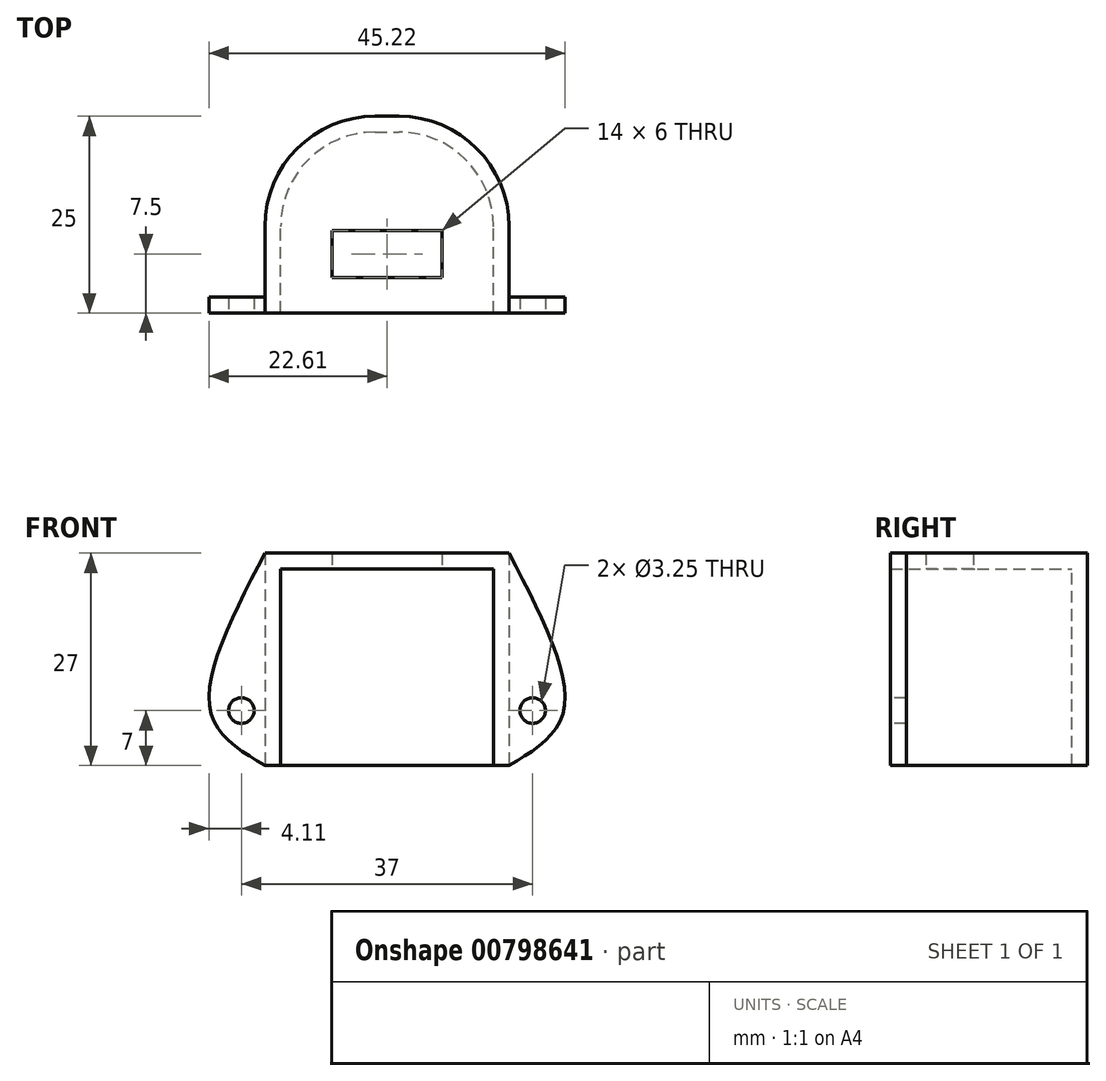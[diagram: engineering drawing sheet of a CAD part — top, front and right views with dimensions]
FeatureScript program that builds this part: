
annotation { "Feature Type Name" : "Feature", "Feature Type Description" : "" }
export const myFeature = defineFeature(function(context is Context, id is Id, definition is map)
    precondition{}
    {
        {
            var Q0;
            Q0=qCreatedBy(makeId("Top.planeOp"),FACE);
            var sketch = newSketch(context, id + "F0", { "sketchPlane" : qUnion([Q0])});
            skLineSegment(sketch, "E0.top", {"start": v(12, 23) * mm, "end": v(15, 23) * mm});
            skLineSegment(sketch, "E0.left", {"start": v(0, 5) * mm, "end": v(0, 11) * mm});
            skLineSegment(sketch, "E0.right", {"start": v(27, 5) * mm, "end": v(27, 11) * mm});
            skPoint(sketch, "E1.visualSharp", {"position": v(0, 23) * mm});
            skArc(sketch, "E1.filletArc", {"start": v(12, 23) * mm, "mid": v(3.51, 19.49) * mm, "end": v(0, 11) * mm});
            skPoint(sketch, "E2.visualSharp", {"position": v(27, 23) * mm});
            skArc(sketch, "E2.filletArc", {"start": v(27, 11) * mm, "mid": v(23.49, 19.49) * mm, "end": v(15, 23) * mm});
            skPoint(sketch, "E3.visualSharp", {"position": v(27, 0) * mm});
            skPoint(sketch, "E4.visualSharp", {"position": v(0, 0) * mm});
            skLineSegment(sketch, "E5.2", {"start": v(-2, 5) * mm, "end": v(-2, 11) * mm});
            skArc(sketch, "E5.4", {"start": v(12, 25) * mm, "mid": v(2.1, 20.9) * mm, "end": v(-2, 11) * mm});
            skLineSegment(sketch, "E5.5", {"start": v(12, 25) * mm, "end": v(15, 25) * mm});
            skArc(sketch, "E5.6", {"start": v(29, 11) * mm, "mid": v(24.9, 20.9) * mm, "end": v(15, 25) * mm});
            skLineSegment(sketch, "E5.7", {"start": v(29, 5) * mm, "end": v(29, 11) * mm});
            skLineSegment(sketch, "E6.bottom", {"start": v(6.5, 10.5) * mm, "end": v(20.5, 10.5) * mm});
            skLineSegment(sketch, "E6.top", {"start": v(6.5, 4.5) * mm, "end": v(20.5, 4.5) * mm});
            skLineSegment(sketch, "E6.left", {"start": v(6.5, 10.5) * mm, "end": v(6.5, 4.5) * mm});
            skLineSegment(sketch, "E6.right", {"start": v(20.5, 10.5) * mm, "end": v(20.5, 4.5) * mm});
            skLineSegment(sketch, "E7", {"start": v(-2, 5) * mm, "end": v(-2, 0) * mm});
            skLineSegment(sketch, "E8", {"start": v(29, 0) * mm, "end": v(29, 5) * mm});
            skLineSegment(sketch, "E9", {"start": v(0, 5) * mm, "end": v(0, 0) * mm});
            skLineSegment(sketch, "E10", {"start": v(0, 0) * mm, "end": v(-2, 0) * mm});
            skLineSegment(sketch, "E11", {"start": v(27, 5) * mm, "end": v(27, 0) * mm});
            skLineSegment(sketch, "E12", {"start": v(27, 0) * mm, "end": v(29, 0) * mm});
            skPoint(sketch, "E13.orphan", {"position": v(29, -2) * mm});
            skLineSegment(sketch, "E14", {"start": v(0, 0) * mm, "end": v(27, 0) * mm});
            skSolve(sketch);
        }
        {
            var Q0;
            Q0=makeQuery(id+"F0.imprint","IMPRINT",FACE,{"disambiguationData":[TD([[makeQuery(id+"F0.imprint","IMPRINT",EDGE,{"derivedFrom":sQuery(id+"F0.wireOp",EDGE,"E0.top")}),1.0]])]});
            var Q1;
            Q1=makeQuery(id+"F0.imprint","IMPRINT",FACE,{"disambiguationData":[TD([[makeQuery(id+"F0.imprint","IMPRINT",EDGE,{"derivedFrom":sQuery(id+"F0.wireOp",EDGE,"E0.top")}),-1.0]])]});
            extrude(context, id + "F1", {"entities" : qUnion([Q0, Q1]), "depth" : 2 * mm, "offsetDistance" : 25 * mm});
        }
        {
            var Q0;
            Q0=makeQuery(id+"F1.opExtrude","CAP_FACE",FACE,{"disambiguationData":[OSD([sQuery(id+"F0.wireOp",EDGE,"E0.bottom"),sQuery(id+"F0.wireOp",EDGE,"E0.top"),sQuery(id+"F0.wireOp",EDGE,"E0.left"),sQuery(id+"F0.wireOp",EDGE,"E0.right"),sQuery(id+"F0.wireOp",EDGE,"E1.filletArc"),sQuery(id+"F0.wireOp",EDGE,"E2.filletArc"),sQuery(id+"F0.wireOp",EDGE,"E6.bottom"),sQuery(id+"F0.wireOp",EDGE,"E6.top"),sQuery(id+"F0.wireOp",EDGE,"E6.left"),sQuery(id+"F0.wireOp",EDGE,"E6.right"),sQuery(id+"F0.wireOp",EDGE,"E9"),sQuery(id+"F0.wireOp",EDGE,"LHaNOpJJ-Fasi-Yn89-1YLt-XwrULM0i3jNw"),sQuery(id+"F0.wireOp",EDGE,"VzsqZfYQ-e0Jo-APly-HRyu-TeHSbx14rwkw"),sQuery(id+"F0.wireOp",EDGE,"E11")])],"isStart":true});
            var sketch = newSketch(context, id + "F2", { "sketchPlane" : qUnion([Q0])});
            skLineSegment(sketch, "E15.0", {"start": v(0, 0) * mm, "end": v(0, -11) * mm});
            skLineSegment(sketch, "E15.1", {"start": v(27, 0) * mm, "end": v(27, -11) * mm});
            skArc(sketch, "E15.2", {"start": v(27, -11) * mm, "mid": v(23.49, -19.49) * mm, "end": v(15, -23) * mm});
            skLineSegment(sketch, "E15.3", {"start": v(12, -23) * mm, "end": v(15, -23) * mm});
            skArc(sketch, "E15.4", {"start": v(12, -23) * mm, "mid": v(3.51, -19.49) * mm, "end": v(0, -11) * mm});
            skSolve(sketch);
        }
        {
            var Q0;
            {var subQ2=sQuery(id+"F2.wireOp",EDGE,"E15.0");Q0=makeQuery(id+"F2.imprint","IMPRINT",FACE,{"disambiguationData":[TD([[makeQuery(id+"F2.imprint","IMPRINT",EDGE,{"derivedFrom":subQ2}),-1.0]])]});}
            extrude(context, id + "F3", {"entities" : qUnion([Q0]), "operationType" : NewBodyOperationType.ADD, "depth" : 25 * mm, "offsetDistance" : 25 * mm});
        }
        {
            var Q0;
            {var subQ0=sQuery(id+"F0.wireOp",EDGE,"E14");var subQ1=sQuery(id+"F0.wireOp",EDGE,"E12");var subQ2=sQuery(id+"F0.wireOp",EDGE,"E10");var subQ3=makeQuery(id+"F1.opExtrude","CAP_EDGE",EDGE,{"disambiguationData":[OSD([subQ2,subQ1,subQ0])],"isStart":true});Q0=makeQuery(id+"F3.boolean.opBoolean","MERGE",FACE,{"derivedFrom":[makeQuery(id+"F1.opExtrude","SWEPT_FACE",FACE,{"disambiguationData":[OSD([subQ2,subQ1,subQ0])]}),makeQuery(id+"F3.opExtrude","SWEPT_FACE",FACE,{"disambiguationData":[OSD([subQ2,subQ1,subQ0]),TDD([makeQuery(id+"F2.imprint","IMPRINT",EDGE,{"disambiguationData":[TD([[makeQuery(id+"F2.imprint","INTERSECT",VERTEX,{"derivedFrom":[subQ3,sQuery(id+"F2.wireOp",EDGE,"E15.0")]}),-1.0]])],"derivedFrom":subQ3})])]}),makeQuery(id+"F3.opExtrude","SWEPT_FACE",FACE,{"disambiguationData":[OSD([subQ2,subQ1,subQ0]),TDD([makeQuery(id+"F2.imprint","IMPRINT",EDGE,{"disambiguationData":[TD([[makeQuery(id+"F2.imprint","INTERSECT",VERTEX,{"derivedFrom":[subQ3,sQuery(id+"F2.wireOp",EDGE,"E15.1")]}),1.0]])],"derivedFrom":subQ3})])]})]});}
            var sketch = newSketch(context, id + "F4", { "sketchPlane" : qUnion([Q0])});
            skCircle(sketch, "E16", {"center": v(32, -18) * mm, "radius": 1.63 * mm});
            skCircle(sketch, "E17", {"center": v(-5, -18) * mm, "radius": 1.63 * mm});
            skFitSpline(sketch, "E18", {"points": [v(29, 2) * mm, v(35.93, -18.1) * mm, v(29, -25) * mm], "startDerivative": vector(20.2, -38.71) * mm, "endDerivative": vector(-22.97, -13.69) * mm});
            skFitSpline(sketch, "E19", {"points": [v(-2, 2) * mm, v(-8.93, -18.1) * mm, v(-2, -25) * mm], "startDerivative": vector(-20.2, -38.71) * mm, "endDerivative": vector(22.97, -13.69) * mm});
            skLineSegment(sketch, "E20", {"start": v(13.5, 2) * mm, "end": v(13.5, -30.7) * mm, "construction": true});
            skSolve(sketch);
        }
        {
            var Q0;
            Q0=makeQuery(id+"F4.imprint","IMPRINT",FACE,{"disambiguationData":[TD([[makeQuery(id+"F4.imprint","IMPRINT",EDGE,{"derivedFrom":sQuery(id+"F4.wireOp",EDGE,"E16")}),-1.0]])]});
            var Q1;
            Q1=makeQuery(id+"F4.imprint","IMPRINT",FACE,{"disambiguationData":[TD([[makeQuery(id+"F4.imprint","IMPRINT",EDGE,{"derivedFrom":sQuery(id+"F4.wireOp",EDGE,"E17")}),-1.0]])]});
            extrude(context, id + "F5", {"entities" : qUnion([Q0, Q1]), "operationType" : NewBodyOperationType.ADD, "depth" : -2 * mm, "offsetDistance" : 25 * mm});
        }
    });
